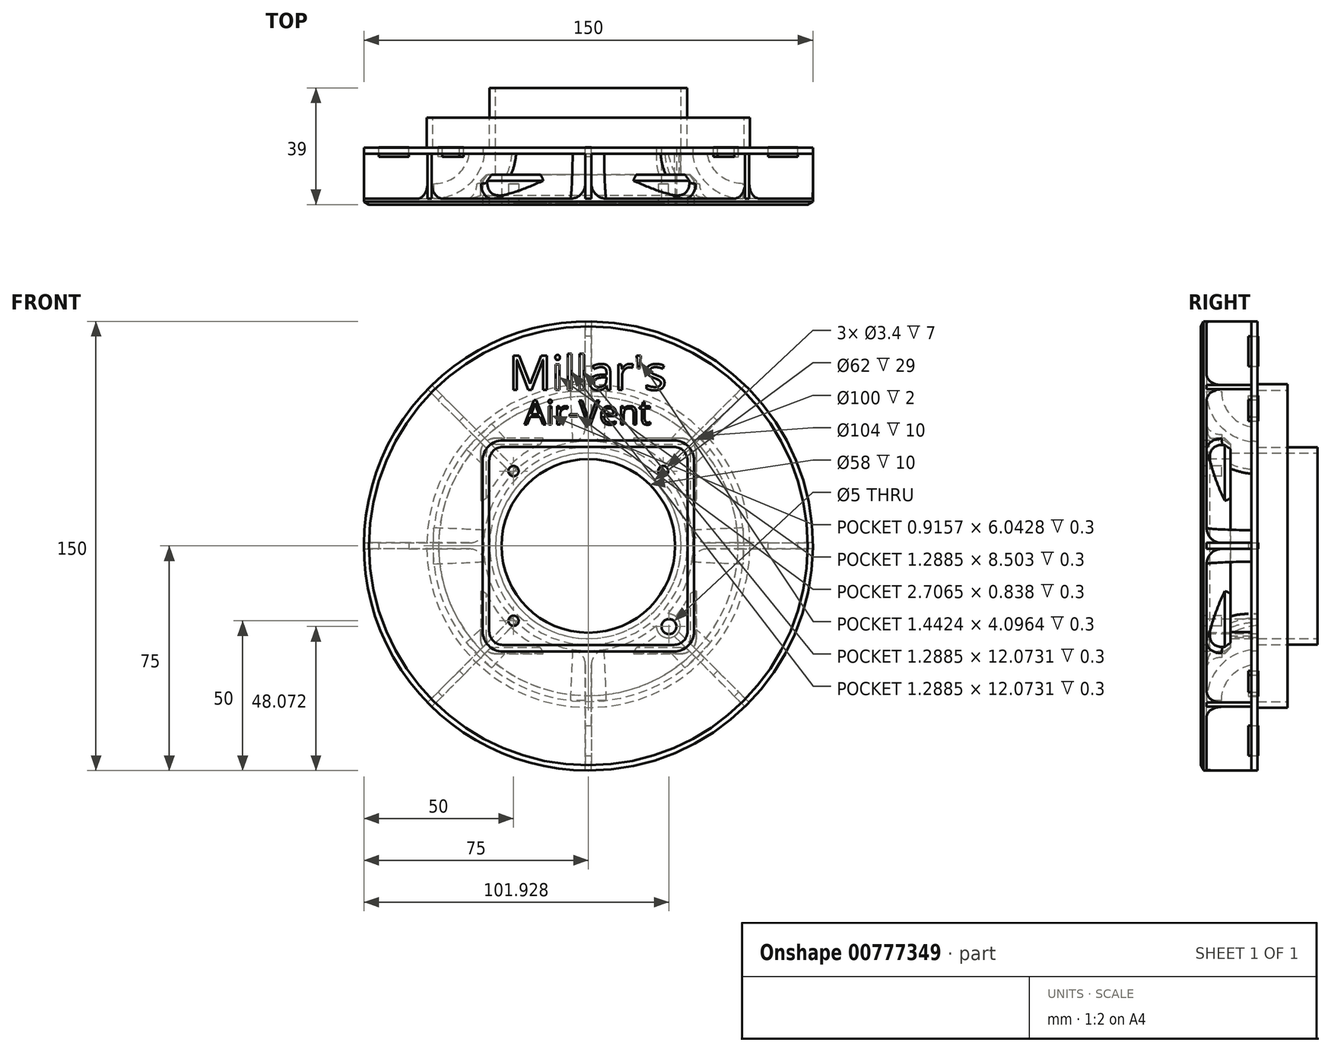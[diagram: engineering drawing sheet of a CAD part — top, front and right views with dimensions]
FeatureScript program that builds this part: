
annotation { "Feature Type Name" : "Feature", "Feature Type Description" : "" }
export const myFeature = defineFeature(function(context is Context, id is Id, definition is map)
    precondition{}
    {
        {
            var Q0;
            Q0=qCreatedBy(makeId("Right.planeOp"),FACE);
            var sketch = newSketch(context, id + "F0", { "sketchPlane" : qUnion([Q0])});
            skLineSegment(sketch, "E0", {"start": v(20, 33) * mm, "end": v(0, 33) * mm});
            skLineSegment(sketch, "E1", {"start": v(0, 33) * mm, "end": v(0, 35) * mm});
            skLineSegment(sketch, "E2", {"start": v(20, 33) * mm, "end": v(20, 31) * mm});
            skLineSegment(sketch, "E3", {"start": v(20, 31) * mm, "end": v(0, 31) * mm});
            skArc(sketch, "E4", {"start": v(0, 35) * mm, "mid": v(-12.02, 39.98) * mm, "end": v(-17, 52) * mm});
            skLineSegment(sketch, "E5", {"start": v(0, 50) * mm, "end": v(0, 52) * mm});
            skLineSegment(sketch, "E6", {"start": v(0, 52) * mm, "end": v(10, 52) * mm});
            skLineSegment(sketch, "E7", {"start": v(10, 52) * mm, "end": v(10, 54) * mm});
            skLineSegment(sketch, "E8", {"start": v(10, 54) * mm, "end": v(0, 54) * mm});
            skLineSegment(sketch, "E9", {"start": v(0, 54) * mm, "end": v(0, 75) * mm});
            skLineSegment(sketch, "E10", {"start": v(0, 75) * mm, "end": v(-2, 75) * mm});
            skLineSegment(sketch, "E11", {"start": v(-2, 75) * mm, "end": v(-2, 50) * mm});
            skLineSegment(sketch, "E12", {"start": v(-2, 50) * mm, "end": v(0, 50) * mm});
            skLineSegment(sketch, "E13", {"start": v(-17, 52) * mm, "end": v(-17, 75) * mm});
            skLineSegment(sketch, "E14", {"start": v(-17, 75) * mm, "end": v(-19, 75) * mm});
            skLineSegment(sketch, "E15", {"start": v(-19, 75) * mm, "end": v(-19, 31) * mm});
            skLineSegment(sketch, "E16", {"start": v(0, 0) * mm, "end": v(-26.64, 0) * mm, "construction": true});
            skLineSegment(sketch, "E17", {"start": v(0, 31) * mm, "end": v(-19, 31) * mm});
            skSolve(sketch);
        }
        {
            var Q0;
            Q0=makeQuery(id+"F0.imprint","IMPRINT",FACE,{"disambiguationData":[TD([[makeQuery(id+"F0.imprint","IMPRINT",EDGE,{"derivedFrom":sQuery(id+"F0.wireOp",EDGE,"E0")}),1.0]])]});
            var Q1;
            Q1=makeQuery(id+"F0.imprint","IMPRINT",FACE,{"disambiguationData":[TD([[makeQuery(id+"F0.imprint","IMPRINT",EDGE,{"derivedFrom":sQuery(id+"F0.wireOp",EDGE,"E5")}),1.0]])]});
            var Q2;
            Q2=sQuery(id+"F0.wireOp",EDGE,"E16");
            revolve(context, id + "F1", {"surfaceOperationType" : NewSurfaceOperationType.NEW, "entities" : qUnion([Q0, Q1]), "axis" : qUnion([Q2]), "revolveType" : RevolveType.FULL});
        }
        {
            var Q0;
            Q0=qCreatedBy(makeId("Front.planeOp"),FACE);
            var Q1;
            Q1 = qBodyType(qCreatedBy(id + "F3" ,EDGE), BodyType.WIRE);
            cPlane(context, id + "F2", {"entities" : qUnion([Q0, Q1]), "cplaneType" : CPlaneType.OFFSET, "offset" : 19 * mm, "width" : 150 * mm, "height" : 150 * mm});
        }
        {
            var Q0;
            Q0=qCreatedBy(id+"F2.planeOp",FACE);
            var sketch = newSketch(context, id + "F3", { "sketchPlane" : qUnion([Q0])});
            skLineSegment(sketch, "E18.bottom", {"start": v(31, 36) * mm, "end": v(-31, 36) * mm});
            skLineSegment(sketch, "E18.top", {"start": v(31, -36) * mm, "end": v(-31, -36) * mm});
            skLineSegment(sketch, "E18.left", {"start": v(36, 31) * mm, "end": v(36, -31) * mm});
            skLineSegment(sketch, "E18.right", {"start": v(-36, 31) * mm, "end": v(-36, -31) * mm});
            skPoint(sketch, "E18.middle", {"position": v(0, 0) * mm});
            skPoint(sketch, "E19.visualSharp", {"position": v(-36, 36) * mm});
            skArc(sketch, "E19.filletArc", {"start": v(-31, 36) * mm, "mid": v(-34.54, 34.54) * mm, "end": v(-36, 31) * mm});
            skPoint(sketch, "E20.visualSharp", {"position": v(36, 36) * mm});
            skArc(sketch, "E20.filletArc", {"start": v(36, 31) * mm, "mid": v(34.54, 34.54) * mm, "end": v(31, 36) * mm});
            skPoint(sketch, "E21.visualSharp", {"position": v(36, -36) * mm});
            skArc(sketch, "E21.filletArc", {"start": v(31, -36) * mm, "mid": v(34.54, -34.54) * mm, "end": v(36, -31) * mm});
            skPoint(sketch, "E22.visualSharp", {"position": v(-36, -36) * mm});
            skArc(sketch, "E22.filletArc", {"start": v(-36, -31) * mm, "mid": v(-34.54, -34.54) * mm, "end": v(-31, -36) * mm});
            skSolve(sketch);
        }
        {
            var Q0;
            Q0=qCreatedBy(id+"F2.planeOp",FACE);
            var sketch = newSketch(context, id + "F4", { "sketchPlane" : qUnion([Q0])});
            skLineSegment(sketch, "E23", {"start": v(0, 0) * mm, "end": v(0, 79.75) * mm, "construction": true});
            skCircle(sketch, "E24", {"center": v(0, 0) * mm, "radius": 35 * mm, "construction": true});
            skCircle(sketch, "E25", {"center": v(0, 0) * mm, "radius": 75 * mm, "construction": true});
            skLineSegment(sketch, "E26", {"start": v(1, 34.99) * mm, "end": v(1, 75) * mm});
            skLineSegment(sketch, "E27", {"start": v(1, 75) * mm, "end": v(-1, 75) * mm});
            skLineSegment(sketch, "E28", {"start": v(-1, 75) * mm, "end": v(-1, 34.99) * mm});
            skLineSegment(sketch, "E29", {"start": v(-1, 34.99) * mm, "end": v(1, 34.99) * mm});
            skLineSegment(sketch, "E30.1.0", {"start": v(-24.03, 25.45) * mm, "end": v(-52.32, 53.74) * mm});
            skLineSegment(sketch, "E30.1.1", {"start": v(-52.32, 53.74) * mm, "end": v(-53.74, 52.32) * mm});
            skLineSegment(sketch, "E30.1.2", {"start": v(-53.74, 52.32) * mm, "end": v(-25.45, 24.03) * mm});
            skLineSegment(sketch, "E30.1.3", {"start": v(-25.45, 24.03) * mm, "end": v(-24.03, 25.45) * mm});
            skLineSegment(sketch, "E30.2.0", {"start": v(-34.99, 1) * mm, "end": v(-75, 1) * mm});
            skLineSegment(sketch, "E30.2.1", {"start": v(-75, 1) * mm, "end": v(-75, -1) * mm});
            skLineSegment(sketch, "E30.2.2", {"start": v(-75, -1) * mm, "end": v(-34.99, -1) * mm});
            skLineSegment(sketch, "E30.2.3", {"start": v(-34.99, -1) * mm, "end": v(-34.99, 1) * mm});
            skLineSegment(sketch, "E30.3.0", {"start": v(-25.45, -24.03) * mm, "end": v(-53.74, -52.32) * mm});
            skLineSegment(sketch, "E30.3.1", {"start": v(-53.74, -52.32) * mm, "end": v(-52.32, -53.74) * mm});
            skLineSegment(sketch, "E30.3.2", {"start": v(-52.32, -53.74) * mm, "end": v(-24.03, -25.45) * mm});
            skLineSegment(sketch, "E30.3.3", {"start": v(-24.03, -25.45) * mm, "end": v(-25.45, -24.03) * mm});
            skLineSegment(sketch, "E30.4.0", {"start": v(-1, -34.99) * mm, "end": v(-1, -75) * mm});
            skLineSegment(sketch, "E30.4.1", {"start": v(-1, -75) * mm, "end": v(1, -75) * mm});
            skLineSegment(sketch, "E30.4.2", {"start": v(1, -75) * mm, "end": v(1, -34.99) * mm});
            skLineSegment(sketch, "E30.4.3", {"start": v(1, -34.99) * mm, "end": v(-1, -34.99) * mm});
            skLineSegment(sketch, "E30.5.0", {"start": v(24.03, -25.45) * mm, "end": v(52.32, -53.74) * mm});
            skLineSegment(sketch, "E30.5.1", {"start": v(52.32, -53.74) * mm, "end": v(53.74, -52.32) * mm});
            skLineSegment(sketch, "E30.5.2", {"start": v(53.74, -52.32) * mm, "end": v(25.45, -24.03) * mm});
            skLineSegment(sketch, "E30.5.3", {"start": v(25.45, -24.03) * mm, "end": v(24.03, -25.45) * mm});
            skLineSegment(sketch, "E30.6.0", {"start": v(34.99, -1) * mm, "end": v(75, -1) * mm});
            skLineSegment(sketch, "E30.6.1", {"start": v(75, -1) * mm, "end": v(75, 1) * mm});
            skLineSegment(sketch, "E30.6.2", {"start": v(75, 1) * mm, "end": v(34.99, 1) * mm});
            skLineSegment(sketch, "E30.6.3", {"start": v(34.99, 1) * mm, "end": v(34.99, -1) * mm});
            skLineSegment(sketch, "E30.7.0", {"start": v(25.45, 24.03) * mm, "end": v(53.74, 52.32) * mm});
            skLineSegment(sketch, "E30.7.1", {"start": v(53.74, 52.32) * mm, "end": v(52.32, 53.74) * mm});
            skLineSegment(sketch, "E30.7.2", {"start": v(52.32, 53.74) * mm, "end": v(24.03, 25.45) * mm});
            skLineSegment(sketch, "E30.7.3", {"start": v(24.03, 25.45) * mm, "end": v(25.45, 24.03) * mm});
            skSolve(sketch);
        }
        {
            var Q0;
            Q0=makeQuery(id+"F4.imprint","IMPRINT",FACE,{"disambiguationData":[TD([[makeQuery(id+"F4.imprint","IMPRINT",EDGE,{"derivedFrom":sQuery(id+"F4.wireOp",EDGE,"E30.1.0")}),1.0]])]});
            var Q1;
            Q1=makeQuery(id+"F4.imprint","IMPRINT",FACE,{"disambiguationData":[TD([[makeQuery(id+"F4.imprint","IMPRINT",EDGE,{"derivedFrom":sQuery(id+"F4.wireOp",EDGE,"E30.2.0")}),1.0]])]});
            var Q2;
            Q2=makeQuery(id+"F4.imprint","IMPRINT",FACE,{"disambiguationData":[TD([[makeQuery(id+"F4.imprint","IMPRINT",EDGE,{"derivedFrom":sQuery(id+"F4.wireOp",EDGE,"E30.3.0")}),1.0]])]});
            var Q3;
            Q3=makeQuery(id+"F4.imprint","IMPRINT",FACE,{"disambiguationData":[TD([[makeQuery(id+"F4.imprint","IMPRINT",EDGE,{"derivedFrom":sQuery(id+"F4.wireOp",EDGE,"E30.4.0")}),1.0]])]});
            var Q4;
            Q4=makeQuery(id+"F4.imprint","IMPRINT",FACE,{"disambiguationData":[TD([[makeQuery(id+"F4.imprint","IMPRINT",EDGE,{"derivedFrom":sQuery(id+"F4.wireOp",EDGE,"E30.5.0")}),1.0]])]});
            var Q5;
            Q5=makeQuery(id+"F4.imprint","IMPRINT",FACE,{"disambiguationData":[TD([[makeQuery(id+"F4.imprint","IMPRINT",EDGE,{"derivedFrom":sQuery(id+"F4.wireOp",EDGE,"E30.6.0")}),1.0]])]});
            var Q6;
            Q6=makeQuery(id+"F4.imprint","IMPRINT",FACE,{"disambiguationData":[TD([[makeQuery(id+"F4.imprint","IMPRINT",EDGE,{"derivedFrom":sQuery(id+"F4.wireOp",EDGE,"E30.7.0")}),1.0]])]});
            var Q7;
            Q7=makeQuery(id+"F4.imprint","IMPRINT",FACE,{"disambiguationData":[TD([[makeQuery(id+"F4.imprint","IMPRINT",EDGE,{"derivedFrom":sQuery(id+"F4.wireOp",EDGE,"E26")}),1.0]])]});
            extrude(context, id + "F5", {"entities" : qUnion([Q0, Q1, Q2, Q3, Q4, Q5, Q6, Q7]), "operationType" : NewBodyOperationType.ADD, "oppositeDirection" : true, "depth" : 17 * mm, "offsetDistance" : 25 * mm});
        }
        {
            var Q0;
            Q0=qCreatedBy(id+"F2.planeOp",FACE);
            cPlane(context, id + "F6", {"entities" : qUnion([Q0]), "cplaneType" : CPlaneType.OFFSET, "offset" : 17 * mm, "oppositeDirection" : true, "width" : 150 * mm, "height" : 150 * mm});
        }
        {
            var Q0;
            Q0=qCreatedBy(id+"F6.planeOp",FACE);
            var sketch = newSketch(context, id + "F7", { "sketchPlane" : qUnion([Q0])});
            skLineSegment(sketch, "E31", {"start": v(0, 0) * mm, "end": v(0, 49.28) * mm, "construction": true});
            skLineSegment(sketch, "E32.bottom", {"start": v(-1, 60) * mm, "end": v(1, 60) * mm});
            skLineSegment(sketch, "E32.top", {"start": v(-1, 70) * mm, "end": v(1, 70) * mm});
            skLineSegment(sketch, "E32.left", {"start": v(-1, 60) * mm, "end": v(-1, 70) * mm});
            skLineSegment(sketch, "E32.right", {"start": v(1, 60) * mm, "end": v(1, 70) * mm});
            skPoint(sketch, "E32.middle", {"position": v(0, 65) * mm});
            skLineSegment(sketch, "E33.1.0", {"start": v(-41.72, 43.13) * mm, "end": v(-48.8, 50.2) * mm});
            skLineSegment(sketch, "E33.1.1", {"start": v(-50.2, 48.8) * mm, "end": v(-48.8, 50.2) * mm});
            skLineSegment(sketch, "E33.1.2", {"start": v(-43.13, 41.72) * mm, "end": v(-50.2, 48.8) * mm});
            skLineSegment(sketch, "E33.1.3", {"start": v(-43.13, 41.72) * mm, "end": v(-41.72, 43.13) * mm});
            skLineSegment(sketch, "E33.2.0", {"start": v(-60, 1) * mm, "end": v(-70, 1) * mm});
            skLineSegment(sketch, "E33.2.1", {"start": v(-70, -1) * mm, "end": v(-70, 1) * mm});
            skLineSegment(sketch, "E33.2.2", {"start": v(-60, -1) * mm, "end": v(-70, -1) * mm});
            skLineSegment(sketch, "E33.2.3", {"start": v(-60, -1) * mm, "end": v(-60, 1) * mm});
            skLineSegment(sketch, "E33.3.0", {"start": v(-43.13, -41.72) * mm, "end": v(-50.2, -48.8) * mm});
            skLineSegment(sketch, "E33.3.1", {"start": v(-48.8, -50.2) * mm, "end": v(-50.2, -48.8) * mm});
            skLineSegment(sketch, "E33.3.2", {"start": v(-41.72, -43.13) * mm, "end": v(-48.8, -50.2) * mm});
            skLineSegment(sketch, "E33.3.3", {"start": v(-41.72, -43.13) * mm, "end": v(-43.13, -41.72) * mm});
            skLineSegment(sketch, "E33.4.0", {"start": v(-1, -60) * mm, "end": v(-1, -70) * mm});
            skLineSegment(sketch, "E33.4.1", {"start": v(1, -70) * mm, "end": v(-1, -70) * mm});
            skLineSegment(sketch, "E33.4.2", {"start": v(1, -60) * mm, "end": v(1, -70) * mm});
            skLineSegment(sketch, "E33.4.3", {"start": v(1, -60) * mm, "end": v(-1, -60) * mm});
            skLineSegment(sketch, "E33.5.0", {"start": v(41.72, -43.13) * mm, "end": v(48.8, -50.2) * mm});
            skLineSegment(sketch, "E33.5.1", {"start": v(50.2, -48.8) * mm, "end": v(48.8, -50.2) * mm});
            skLineSegment(sketch, "E33.5.2", {"start": v(43.13, -41.72) * mm, "end": v(50.2, -48.8) * mm});
            skLineSegment(sketch, "E33.5.3", {"start": v(43.13, -41.72) * mm, "end": v(41.72, -43.13) * mm});
            skLineSegment(sketch, "E33.6.0", {"start": v(60, -1) * mm, "end": v(70, -1) * mm});
            skLineSegment(sketch, "E33.6.1", {"start": v(70, 1) * mm, "end": v(70, -1) * mm});
            skLineSegment(sketch, "E33.6.2", {"start": v(60, 1) * mm, "end": v(70, 1) * mm});
            skLineSegment(sketch, "E33.6.3", {"start": v(60, 1) * mm, "end": v(60, -1) * mm});
            skLineSegment(sketch, "E33.7.0", {"start": v(43.13, 41.72) * mm, "end": v(50.2, 48.8) * mm});
            skLineSegment(sketch, "E33.7.1", {"start": v(48.8, 50.2) * mm, "end": v(50.2, 48.8) * mm});
            skLineSegment(sketch, "E33.7.2", {"start": v(41.72, 43.13) * mm, "end": v(48.8, 50.2) * mm});
            skLineSegment(sketch, "E33.7.3", {"start": v(41.72, 43.13) * mm, "end": v(43.13, 41.72) * mm});
            skPoint(sketch, "E33.center", {"position": v(0, 0) * mm});
            skSolve(sketch);
        }
        {
            var Q0;
            Q0=makeQuery(id+"F7.imprint","IMPRINT",FACE,{"disambiguationData":[TD([[makeQuery(id+"F7.imprint","IMPRINT",EDGE,{"derivedFrom":sQuery(id+"F7.wireOp",EDGE,"E32.bottom")}),1.0]])]});
            var Q1;
            Q1=makeQuery(id+"F7.imprint","IMPRINT",FACE,{"disambiguationData":[TD([[makeQuery(id+"F7.imprint","IMPRINT",EDGE,{"derivedFrom":sQuery(id+"F7.wireOp",EDGE,"E33.7.0")}),1.0]])]});
            var Q2;
            Q2=makeQuery(id+"F7.imprint","IMPRINT",FACE,{"disambiguationData":[TD([[makeQuery(id+"F7.imprint","IMPRINT",EDGE,{"derivedFrom":sQuery(id+"F7.wireOp",EDGE,"E33.6.0")}),1.0]])]});
            var Q3;
            Q3=makeQuery(id+"F7.imprint","IMPRINT",FACE,{"disambiguationData":[TD([[makeQuery(id+"F7.imprint","IMPRINT",EDGE,{"derivedFrom":sQuery(id+"F7.wireOp",EDGE,"E33.1.0")}),1.0]])]});
            var Q4;
            Q4=makeQuery(id+"F7.imprint","IMPRINT",FACE,{"disambiguationData":[TD([[makeQuery(id+"F7.imprint","IMPRINT",EDGE,{"derivedFrom":sQuery(id+"F7.wireOp",EDGE,"E33.2.0")}),1.0]])]});
            var Q5;
            Q5=makeQuery(id+"F7.imprint","IMPRINT",FACE,{"disambiguationData":[TD([[makeQuery(id+"F7.imprint","IMPRINT",EDGE,{"derivedFrom":sQuery(id+"F7.wireOp",EDGE,"E33.3.0")}),1.0]])]});
            var Q6;
            Q6=makeQuery(id+"F7.imprint","IMPRINT",FACE,{"disambiguationData":[TD([[makeQuery(id+"F7.imprint","IMPRINT",EDGE,{"derivedFrom":sQuery(id+"F7.wireOp",EDGE,"E33.4.0")}),1.0]])]});
            var Q7;
            Q7=makeQuery(id+"F7.imprint","IMPRINT",FACE,{"disambiguationData":[TD([[makeQuery(id+"F7.imprint","IMPRINT",EDGE,{"derivedFrom":sQuery(id+"F7.wireOp",EDGE,"E33.5.0")}),1.0]])]});
            extrude(context, id + "F8", {"entities" : qUnion([Q0, Q1, Q2, Q3, Q4, Q5, Q6, Q7]), "operationType" : NewBodyOperationType.ADD, "oppositeDirection" : true, "depth" : 2.2 * mm, "offsetDistance" : 25 * mm});
        }
        {
            var Q0;
            Q0=makeQuery(id+"F3.imprint","IMPRINT",FACE,{"disambiguationData":[TD([[makeQuery(id+"F3.imprint","IMPRINT",EDGE,{"derivedFrom":sQuery(id+"F3.wireOp",EDGE,"E18.bottom")}),1.0]])]});
            extrude(context, id + "F9", {"entities" : qUnion([Q0]), "operationType" : NewBodyOperationType.ADD, "oppositeDirection" : true, "depth" : 10 * mm, "offsetDistance" : 25 * mm});
        }
        {
            var Q0;
            Q0=qCreatedBy(makeId("Front.planeOp"),FACE);
            cPlane(context, id + "F10", {"entities" : qUnion([Q0]), "cplaneType" : CPlaneType.OFFSET, "offset" : 19 * mm, "width" : 150 * mm, "height" : 150 * mm});
        }
        {
            var Q0;
            Q0=qCreatedBy(id+"F10.planeOp",FACE);
            var sketch = newSketch(context, id + "F11", { "sketchPlane" : qUnion([Q0])});
            skLineSegment(sketch, "E34", {"start": v(0, 0) * mm, "end": v(-52.1, 52.1) * mm, "construction": true});
            skLineSegment(sketch, "E35", {"start": v(-52.1, 52.1) * mm, "end": v(0, 0) * mm, "construction": true});
            skLineSegment(sketch, "E36", {"start": v(0, 0) * mm, "end": v(53.31, 53.31) * mm, "construction": true});
            skLineSegment(sketch, "E37", {"start": v(0, 0) * mm, "end": v(0, 62.57) * mm, "construction": true});
            skCircle(sketch, "E38", {"center": v(-25, 25) * mm, "radius": 1.7 * mm});
            skCircle(sketch, "E39.1.0", {"center": v(-25, -25) * mm, "radius": 1.7 * mm});
            skCircle(sketch, "E39.3.0", {"center": v(25, 25) * mm, "radius": 1.7 * mm});
            skPoint(sketch, "E39.center", {"position": v(0, 0) * mm});
            skSolve(sketch);
        }
        {
            var Q0;
            Q0=makeQuery(id+"F11.imprint","IMPRINT",FACE,{"disambiguationData":[TD([[makeQuery(id+"F11.imprint","IMPRINT",EDGE,{"derivedFrom":sQuery(id+"F11.wireOp",EDGE,"E38")}),1.0]])]});
            var Q1;
            Q1=makeQuery(id+"F11.imprint","IMPRINT",FACE,{"disambiguationData":[TD([[makeQuery(id+"F11.imprint","IMPRINT",EDGE,{"derivedFrom":sQuery(id+"F11.wireOp",EDGE,"E39.3.0")}),1.0]])]});
            var Q2;
            Q2=makeQuery(id+"F11.imprint","IMPRINT",FACE,{"disambiguationData":[TD([[makeQuery(id+"F11.imprint","IMPRINT",EDGE,{"derivedFrom":sQuery(id+"F11.wireOp",EDGE,"E39.2.0")}),1.0]])]});
            var Q3;
            Q3=makeQuery(id+"F11.imprint","IMPRINT",FACE,{"disambiguationData":[TD([[makeQuery(id+"F11.imprint","IMPRINT",EDGE,{"derivedFrom":sQuery(id+"F11.wireOp",EDGE,"E39.1.0")}),1.0]])]});
            extrude(context, id + "F12", {"entities" : qUnion([Q0, Q1, Q2, Q3]), "operationType" : NewBodyOperationType.REMOVE, "oppositeDirection" : true, "depth" : 7 * mm, "offsetDistance" : 25 * mm});
        }
        {
            var Q0;
            Q0=qCreatedBy(id+"F10.planeOp",FACE);
            var sketch = newSketch(context, id + "F13", { "sketchPlane" : qUnion([Q0])});
            skCircle(sketch, "E40", {"center": v(0, 0) * mm, "radius": 29 * mm});
            skSolve(sketch);
        }
        {
            var Q0;
            Q0=makeQuery(id+"F13.imprint","IMPRINT",FACE,{"disambiguationData":[TD([[makeQuery(id+"F13.imprint","IMPRINT",EDGE,{"derivedFrom":sQuery(id+"F13.wireOp",EDGE,"E40")}),1.0]])]});
            extrude(context, id + "F14", {"entities" : qUnion([Q0]), "operationType" : NewBodyOperationType.REMOVE, "oppositeDirection" : true, "depth" : 10 * mm, "offsetDistance" : 25 * mm});
        }
        {
            var Q0;
            Q0=makeQuery(id+"F14.boolean.opBoolean","COPY",EDGE,{"derivedFrom":makeQuery(id+"F14.opExtrude","CAP_EDGE",EDGE,{"disambiguationData":[OSD([sQuery(id+"F13.wireOp",EDGE,"E40")])],"isStart":false})});
            var Q1;
            Q1=makeQuery(id+"F9.opExtrude","CAP_EDGE",EDGE,{"disambiguationData":[OSD([sQuery(id+"F3.wireOp",EDGE,"E19.filletArc")])],"isStart":false});
            var Q2;
            Q2=makeQuery(id+"F9.opExtrude","CAP_EDGE",EDGE,{"disambiguationData":[OSD([sQuery(id+"F3.wireOp",EDGE,"E20.filletArc")])],"isStart":false});
            var Q3;
            Q3=makeQuery(id+"F9.opExtrude","CAP_EDGE",EDGE,{"disambiguationData":[OSD([sQuery(id+"F3.wireOp",EDGE,"E21.filletArc")])],"isStart":false});
            var Q4;
            Q4=makeQuery(id+"F9.opExtrude","CAP_EDGE",EDGE,{"disambiguationData":[OSD([sQuery(id+"F3.wireOp",EDGE,"E22.filletArc")])],"isStart":false});
            chamfer(context, id + "F15", {"entities" : qUnion([Q0, Q1, Q2, Q3, Q4]), "width" : 2 * mm, "tangentPropagation" : true});
        }
        {
            var Q0;
            Q0=makeQuery(id+"F1.opRevolve","SWEPT_EDGE",EDGE,{"disambiguationData":[OSD([sQuery(id+"F0.wireOp",EDGE,"E14"),sQuery(id+"F0.wireOp",EDGE,"E15")])]});
            chamfer(context, id + "F16", {"entities" : qUnion([Q0]), "chamferType" : ChamferType.OFFSET_ANGLE, "width" : 1 * mm, "oppositeDirection" : false, "angle" : 60 * degree, "tangentPropagation" : true});
        }
        {
            var Q0;
            Q0=qCreatedBy(makeId("Front.planeOp"),FACE);
            var sketch = newSketch(context, id + "F17", { "sketchPlane" : qUnion([Q0])});
            skLineSegment(sketch, "E41", {"start": v(0, 0) * mm, "end": v(0, 49.28) * mm, "construction": true});
            skLineSegment(sketch, "E42.bottom", {"start": v(-1, 60) * mm, "end": v(1, 60) * mm});
            skLineSegment(sketch, "E42.top", {"start": v(-1, 70) * mm, "end": v(1, 70) * mm});
            skLineSegment(sketch, "E42.left", {"start": v(-1, 60) * mm, "end": v(-1, 70) * mm});
            skLineSegment(sketch, "E42.right", {"start": v(1, 60) * mm, "end": v(1, 70) * mm});
            skPoint(sketch, "E42.middle", {"position": v(0, 65) * mm});
            skLineSegment(sketch, "E43.1.0", {"start": v(-41.72, 43.13) * mm, "end": v(-48.8, 50.2) * mm});
            skLineSegment(sketch, "E43.1.1", {"start": v(-50.2, 48.8) * mm, "end": v(-48.8, 50.2) * mm});
            skLineSegment(sketch, "E43.1.2", {"start": v(-43.13, 41.72) * mm, "end": v(-50.2, 48.8) * mm});
            skLineSegment(sketch, "E43.1.3", {"start": v(-43.13, 41.72) * mm, "end": v(-41.72, 43.13) * mm});
            skLineSegment(sketch, "E43.2.0", {"start": v(-60, 1) * mm, "end": v(-70, 1) * mm});
            skLineSegment(sketch, "E43.2.1", {"start": v(-70, -1) * mm, "end": v(-70, 1) * mm});
            skLineSegment(sketch, "E43.2.2", {"start": v(-60, -1) * mm, "end": v(-70, -1) * mm});
            skLineSegment(sketch, "E43.2.3", {"start": v(-60, -1) * mm, "end": v(-60, 1) * mm});
            skLineSegment(sketch, "E43.3.0", {"start": v(-43.13, -41.72) * mm, "end": v(-50.2, -48.8) * mm});
            skLineSegment(sketch, "E43.3.1", {"start": v(-48.8, -50.2) * mm, "end": v(-50.2, -48.8) * mm});
            skLineSegment(sketch, "E43.3.2", {"start": v(-41.72, -43.13) * mm, "end": v(-48.8, -50.2) * mm});
            skLineSegment(sketch, "E43.3.3", {"start": v(-41.72, -43.13) * mm, "end": v(-43.13, -41.72) * mm});
            skLineSegment(sketch, "E43.4.0", {"start": v(-1, -60) * mm, "end": v(-1, -70) * mm});
            skLineSegment(sketch, "E43.4.1", {"start": v(1, -70) * mm, "end": v(-1, -70) * mm});
            skLineSegment(sketch, "E43.4.2", {"start": v(1, -60) * mm, "end": v(1, -70) * mm});
            skLineSegment(sketch, "E43.4.3", {"start": v(1, -60) * mm, "end": v(-1, -60) * mm});
            skLineSegment(sketch, "E43.5.0", {"start": v(41.72, -43.13) * mm, "end": v(48.8, -50.2) * mm});
            skLineSegment(sketch, "E43.5.1", {"start": v(50.2, -48.8) * mm, "end": v(48.8, -50.2) * mm});
            skLineSegment(sketch, "E43.5.2", {"start": v(43.13, -41.72) * mm, "end": v(50.2, -48.8) * mm});
            skLineSegment(sketch, "E43.5.3", {"start": v(43.13, -41.72) * mm, "end": v(41.72, -43.13) * mm});
            skLineSegment(sketch, "E43.6.0", {"start": v(60, -1) * mm, "end": v(70, -1) * mm});
            skLineSegment(sketch, "E43.6.1", {"start": v(70, 1) * mm, "end": v(70, -1) * mm});
            skLineSegment(sketch, "E43.6.2", {"start": v(60, 1) * mm, "end": v(70, 1) * mm});
            skLineSegment(sketch, "E43.6.3", {"start": v(60, 1) * mm, "end": v(60, -1) * mm});
            skLineSegment(sketch, "E43.7.0", {"start": v(43.13, 41.72) * mm, "end": v(50.2, 48.8) * mm});
            skLineSegment(sketch, "E43.7.1", {"start": v(48.8, 50.2) * mm, "end": v(50.2, 48.8) * mm});
            skLineSegment(sketch, "E43.7.2", {"start": v(41.72, 43.13) * mm, "end": v(48.8, 50.2) * mm});
            skLineSegment(sketch, "E43.7.3", {"start": v(41.72, 43.13) * mm, "end": v(43.13, 41.72) * mm});
            skPoint(sketch, "E43.center", {"position": v(0, 0) * mm});
            skSolve(sketch);
        }
        {
            var Q0;
            Q0=makeQuery(id+"F17.imprint","IMPRINT",FACE,{"disambiguationData":[TD([[makeQuery(id+"F17.imprint","IMPRINT",EDGE,{"derivedFrom":sQuery(id+"F17.wireOp",EDGE,"E42.bottom")}),1.0]])]});
            var Q1;
            Q1=makeQuery(id+"F17.imprint","IMPRINT",FACE,{"disambiguationData":[TD([[makeQuery(id+"F17.imprint","IMPRINT",EDGE,{"derivedFrom":sQuery(id+"F17.wireOp",EDGE,"E43.7.0")}),1.0]])]});
            var Q2;
            Q2=makeQuery(id+"F17.imprint","IMPRINT",FACE,{"disambiguationData":[TD([[makeQuery(id+"F17.imprint","IMPRINT",EDGE,{"derivedFrom":sQuery(id+"F17.wireOp",EDGE,"E43.6.0")}),1.0]])]});
            var Q3;
            Q3=makeQuery(id+"F17.imprint","IMPRINT",FACE,{"disambiguationData":[TD([[makeQuery(id+"F17.imprint","IMPRINT",EDGE,{"derivedFrom":sQuery(id+"F17.wireOp",EDGE,"E43.5.0")}),1.0]])]});
            var Q4;
            Q4=makeQuery(id+"F17.imprint","IMPRINT",FACE,{"disambiguationData":[TD([[makeQuery(id+"F17.imprint","IMPRINT",EDGE,{"derivedFrom":sQuery(id+"F17.wireOp",EDGE,"E43.4.0")}),1.0]])]});
            var Q5;
            Q5=makeQuery(id+"F17.imprint","IMPRINT",FACE,{"disambiguationData":[TD([[makeQuery(id+"F17.imprint","IMPRINT",EDGE,{"derivedFrom":sQuery(id+"F17.wireOp",EDGE,"E43.3.0")}),1.0]])]});
            var Q6;
            Q6=makeQuery(id+"F17.imprint","IMPRINT",FACE,{"disambiguationData":[TD([[makeQuery(id+"F17.imprint","IMPRINT",EDGE,{"derivedFrom":sQuery(id+"F17.wireOp",EDGE,"E43.2.0")}),1.0]])]});
            var Q7;
            Q7=makeQuery(id+"F17.imprint","IMPRINT",FACE,{"disambiguationData":[TD([[makeQuery(id+"F17.imprint","IMPRINT",EDGE,{"derivedFrom":sQuery(id+"F17.wireOp",EDGE,"E43.1.0")}),1.0]])]});
            extrude(context, id + "F18", {"entities" : qUnion([Q0, Q1, Q2, Q3, Q4, Q5, Q6, Q7]), "operationType" : NewBodyOperationType.REMOVE, "depth" : 3 * mm, "offsetDistance" : 25 * mm});
        }
        {
            var Q0;
            Q0=qCreatedBy(makeId("Front.planeOp"),FACE);
            cPlane(context, id + "F19", {"entities" : qUnion([Q0]), "cplaneType" : CPlaneType.OFFSET, "offset" : 20 * mm, "width" : 150 * mm, "height" : 150 * mm});
        }
        {
            var Q0;
            Q0=qCreatedBy(id+"F19.planeOp",FACE);
            var sketch = newSketch(context, id + "F20", { "sketchPlane" : qUnion([Q0])});
            skLineSegment(sketch, "E44.bottom", {"start": v(28.6, 33.05) * mm, "end": v(-28.6, 33.05) * mm});
            skLineSegment(sketch, "E44.top", {"start": v(28.6, -33.05) * mm, "end": v(-28.6, -33.05) * mm});
            skLineSegment(sketch, "E44.left", {"start": v(33.1, 28.55) * mm, "end": v(33.1, -28.55) * mm});
            skLineSegment(sketch, "E44.right", {"start": v(-33.1, 28.55) * mm, "end": v(-33.1, -28.55) * mm});
            skPoint(sketch, "E44.middle", {"position": v(0, 0) * mm});
            skPoint(sketch, "E45.visualSharp", {"position": v(-33.1, 33.05) * mm});
            skArc(sketch, "E45.filletArc", {"start": v(-28.6, 33.05) * mm, "mid": v(-31.78, 31.73) * mm, "end": v(-33.1, 28.55) * mm});
            skPoint(sketch, "E46.visualSharp", {"position": v(33.1, 33.05) * mm});
            skArc(sketch, "E46.filletArc", {"start": v(33.1, 28.55) * mm, "mid": v(31.78, 31.73) * mm, "end": v(28.6, 33.05) * mm});
            skPoint(sketch, "E47.visualSharp", {"position": v(33.1, -33.05) * mm});
            skArc(sketch, "E47.filletArc", {"start": v(28.6, -33.05) * mm, "mid": v(31.78, -31.73) * mm, "end": v(33.1, -28.55) * mm});
            skPoint(sketch, "E48.visualSharp", {"position": v(-33.1, -33.05) * mm});
            skArc(sketch, "E48.filletArc", {"start": v(-33.1, -28.55) * mm, "mid": v(-31.78, -31.73) * mm, "end": v(-28.6, -33.05) * mm});
            skArc(sketch, "E49.0", {"start": v(35.3, 28.55) * mm, "mid": v(33.34, 33.29) * mm, "end": v(28.6, 35.25) * mm});
            skLineSegment(sketch, "E49.1", {"start": v(35.3, 28.55) * mm, "end": v(35.3, -28.55) * mm});
            skLineSegment(sketch, "E49.2", {"start": v(28.6, 35.25) * mm, "end": v(-28.6, 35.25) * mm});
            skArc(sketch, "E49.3", {"start": v(28.6, -35.25) * mm, "mid": v(33.34, -33.29) * mm, "end": v(35.3, -28.55) * mm});
            skArc(sketch, "E49.4", {"start": v(-28.6, 35.25) * mm, "mid": v(-33.34, 33.29) * mm, "end": v(-35.3, 28.55) * mm});
            skLineSegment(sketch, "E49.5", {"start": v(-35.3, 28.55) * mm, "end": v(-35.3, -28.55) * mm});
            skArc(sketch, "E49.6", {"start": v(-35.3, -28.55) * mm, "mid": v(-33.34, -33.29) * mm, "end": v(-28.6, -35.25) * mm});
            skLineSegment(sketch, "E49.7", {"start": v(28.6, -35.25) * mm, "end": v(-28.6, -35.25) * mm});
            skSolve(sketch);
        }
        {
            var Q0;
            Q0 = qSketchRegion(id + "F20", true);
            extrude(context, id + "F21", {"entities" : qUnion([Q0]), "operationType" : NewBodyOperationType.REMOVE, "oppositeDirection" : true, "depth" : 4 * mm, "offsetDistance" : 25 * mm});
        }
        {
            var Q0;
            Q0=makeQuery(id+"F5.boolean.opBoolean","INTERSECT",EDGE,{"derivedFrom":[makeQuery(id+"F1.opRevolve","SWEPT_FACE",FACE,{"disambiguationData":[OSD([sQuery(id+"F0.wireOp",EDGE,"E13")])]}),makeQuery(id+"F5.opExtrude","SWEPT_FACE",FACE,{"disambiguationData":[OSD([sQuery(id+"F4.wireOp",EDGE,"E30.7.0")])]})]});
            var Q1;
            Q1=makeQuery(id+"F5.boolean.opBoolean","INTERSECT",EDGE,{"derivedFrom":[makeQuery(id+"F1.opRevolve","SWEPT_FACE",FACE,{"disambiguationData":[OSD([sQuery(id+"F0.wireOp",EDGE,"E13")])]}),makeQuery(id+"F5.opExtrude","SWEPT_FACE",FACE,{"disambiguationData":[OSD([sQuery(id+"F4.wireOp",EDGE,"E26")])]})]});
            var Q2;
            Q2=makeQuery(id+"F5.boolean.opBoolean","INTERSECT",EDGE,{"derivedFrom":[makeQuery(id+"F1.opRevolve","SWEPT_FACE",FACE,{"disambiguationData":[OSD([sQuery(id+"F0.wireOp",EDGE,"E13")])]}),makeQuery(id+"F5.opExtrude","SWEPT_FACE",FACE,{"disambiguationData":[OSD([sQuery(id+"F4.wireOp",EDGE,"E30.6.0")])]})]});
            var Q3;
            Q3=makeQuery(id+"F5.boolean.opBoolean","INTERSECT",EDGE,{"derivedFrom":[makeQuery(id+"F1.opRevolve","SWEPT_FACE",FACE,{"disambiguationData":[OSD([sQuery(id+"F0.wireOp",EDGE,"E13")])]}),makeQuery(id+"F5.opExtrude","SWEPT_FACE",FACE,{"disambiguationData":[OSD([sQuery(id+"F4.wireOp",EDGE,"E30.5.2")])]})]});
            var Q4;
            Q4=makeQuery(id+"F5.boolean.opBoolean","INTERSECT",EDGE,{"derivedFrom":[makeQuery(id+"F1.opRevolve","SWEPT_FACE",FACE,{"disambiguationData":[OSD([sQuery(id+"F0.wireOp",EDGE,"E13")])]}),makeQuery(id+"F5.opExtrude","SWEPT_FACE",FACE,{"disambiguationData":[OSD([sQuery(id+"F4.wireOp",EDGE,"E30.4.2")])]})]});
            var Q5;
            Q5=makeQuery(id+"F5.boolean.opBoolean","INTERSECT",EDGE,{"derivedFrom":[makeQuery(id+"F1.opRevolve","SWEPT_FACE",FACE,{"disambiguationData":[OSD([sQuery(id+"F0.wireOp",EDGE,"E13")])]}),makeQuery(id+"F5.opExtrude","SWEPT_FACE",FACE,{"disambiguationData":[OSD([sQuery(id+"F4.wireOp",EDGE,"E30.3.2")])]})]});
            var Q6;
            Q6=makeQuery(id+"F5.boolean.opBoolean","INTERSECT",EDGE,{"derivedFrom":[makeQuery(id+"F1.opRevolve","SWEPT_FACE",FACE,{"disambiguationData":[OSD([sQuery(id+"F0.wireOp",EDGE,"E13")])]}),makeQuery(id+"F5.opExtrude","SWEPT_FACE",FACE,{"disambiguationData":[OSD([sQuery(id+"F4.wireOp",EDGE,"E30.2.2")])]})]});
            var Q7;
            Q7=makeQuery(id+"F5.boolean.opBoolean","INTERSECT",EDGE,{"derivedFrom":[makeQuery(id+"F1.opRevolve","SWEPT_FACE",FACE,{"disambiguationData":[OSD([sQuery(id+"F0.wireOp",EDGE,"E13")])]}),makeQuery(id+"F5.opExtrude","SWEPT_FACE",FACE,{"disambiguationData":[OSD([sQuery(id+"F4.wireOp",EDGE,"E30.1.0")])]})]});
            var Q8;
            Q8=makeQuery(id+"F5.boolean.opBoolean","INTERSECT",EDGE,{"derivedFrom":[makeQuery(id+"F1.opRevolve","SWEPT_FACE",FACE,{"disambiguationData":[OSD([sQuery(id+"F0.wireOp",EDGE,"E13")])]}),makeQuery(id+"F5.opExtrude","SWEPT_FACE",FACE,{"disambiguationData":[OSD([sQuery(id+"F4.wireOp",EDGE,"E30.6.2")])]})]});
            var Q9;
            Q9=makeQuery(id+"F5.boolean.opBoolean","INTERSECT",EDGE,{"derivedFrom":[makeQuery(id+"F1.opRevolve","SWEPT_FACE",FACE,{"disambiguationData":[OSD([sQuery(id+"F0.wireOp",EDGE,"E13")])]}),makeQuery(id+"F5.opExtrude","SWEPT_FACE",FACE,{"disambiguationData":[OSD([sQuery(id+"F4.wireOp",EDGE,"E30.7.2")])]})]});
            var Q10;
            Q10=makeQuery(id+"F5.boolean.opBoolean","INTERSECT",EDGE,{"derivedFrom":[makeQuery(id+"F1.opRevolve","SWEPT_FACE",FACE,{"disambiguationData":[OSD([sQuery(id+"F0.wireOp",EDGE,"E13")])]}),makeQuery(id+"F5.opExtrude","SWEPT_FACE",FACE,{"disambiguationData":[OSD([sQuery(id+"F4.wireOp",EDGE,"E30.2.0")])]})]});
            var Q11;
            Q11=makeQuery(id+"F5.boolean.opBoolean","INTERSECT",EDGE,{"derivedFrom":[makeQuery(id+"F1.opRevolve","SWEPT_FACE",FACE,{"disambiguationData":[OSD([sQuery(id+"F0.wireOp",EDGE,"E13")])]}),makeQuery(id+"F5.opExtrude","SWEPT_FACE",FACE,{"disambiguationData":[OSD([sQuery(id+"F4.wireOp",EDGE,"E30.3.0")])]})]});
            var Q12;
            Q12=makeQuery(id+"F5.boolean.opBoolean","INTERSECT",EDGE,{"derivedFrom":[makeQuery(id+"F1.opRevolve","SWEPT_FACE",FACE,{"disambiguationData":[OSD([sQuery(id+"F0.wireOp",EDGE,"E13")])]}),makeQuery(id+"F5.opExtrude","SWEPT_FACE",FACE,{"disambiguationData":[OSD([sQuery(id+"F4.wireOp",EDGE,"E30.5.0")])]})]});
            var Q13;
            Q13=makeQuery(id+"F5.boolean.opBoolean","INTERSECT",EDGE,{"derivedFrom":[makeQuery(id+"F1.opRevolve","SWEPT_FACE",FACE,{"disambiguationData":[OSD([sQuery(id+"F0.wireOp",EDGE,"E13")])]}),makeQuery(id+"F5.opExtrude","SWEPT_FACE",FACE,{"disambiguationData":[OSD([sQuery(id+"F4.wireOp",EDGE,"E30.4.0")])]})]});
            var Q14;
            Q14=makeQuery(id+"F5.boolean.opBoolean","INTERSECT",EDGE,{"derivedFrom":[makeQuery(id+"F1.opRevolve","SWEPT_FACE",FACE,{"disambiguationData":[OSD([sQuery(id+"F0.wireOp",EDGE,"E13")])]}),makeQuery(id+"F5.opExtrude","SWEPT_FACE",FACE,{"disambiguationData":[OSD([sQuery(id+"F4.wireOp",EDGE,"E30.1.2")])]})]});
            var Q15;
            Q15=makeQuery(id+"F5.boolean.opBoolean","INTERSECT",EDGE,{"derivedFrom":[makeQuery(id+"F1.opRevolve","SWEPT_FACE",FACE,{"disambiguationData":[OSD([sQuery(id+"F0.wireOp",EDGE,"E13")])]}),makeQuery(id+"F5.opExtrude","SWEPT_FACE",FACE,{"disambiguationData":[OSD([sQuery(id+"F4.wireOp",EDGE,"E28")])]})]});
            fillet(context, id + "F22", {"entities" : qUnion([Q0, Q1, Q2, Q3, Q4, Q5, Q6, Q7, Q8, Q9, Q10, Q11, Q12, Q13, Q14, Q15]), "radius" : 5 * mm, "tangentPropagation" : true, "allowEdgeOverflow" : false});
        }
        {
            var Q0;
            Q0=qCreatedBy(makeId("Front.planeOp"),FACE);
            cPlane(context, id + "F23", {"entities" : qUnion([Q0]), "cplaneType" : CPlaneType.OFFSET, "offset" : 19 * mm, "width" : 150 * mm, "height" : 150 * mm});
        }
        {
            var Q0;
            Q0=qCreatedBy(id+"F23.planeOp",FACE);
            var sketch = newSketch(context, id + "F24", { "sketchPlane" : qUnion([Q0])});
            skText(sketch, "E50", { "text": "Air-Vent", "fontName": "OpenSans-Regular.ttf"});
            skText(sketch, "E51", { "text": "Millar\'s", "fontName": "OpenSans-Regular.ttf"});
            const initialGuessF24  = {"E50": [-0.02135, 0.04056, 1, 0, 0.00813], "E51": [-0.02664, 0.05214, 1, 0, 0.01144]};
            skSetInitialGuess(sketch, initialGuessF24);
            skSolve(sketch);
        }
        {
            var Q0;
            Q0 = qSketchRegion(id + "F24", true);
            extrude(context, id + "F25", {"entities" : qUnion([Q0]), "operationType" : NewBodyOperationType.REMOVE, "oppositeDirection" : true, "depth" : 0.3 * mm, "offsetDistance" : 25 * mm});
        }
        {
            var Q0;
            Q0=qCreatedBy(id+"F23.planeOp",FACE);
            var sketch = newSketch(context, id + "F26", { "sketchPlane" : qUnion([Q0])});
            skCircle(sketch, "E52", {"center": v(26.7, -26.7) * mm, "radius": 4 * mm});
            skLineSegment(sketch, "E53", {"start": v(26.7, -26.7) * mm, "end": v(26.7, 0) * mm, "construction": true});
            skLineSegment(sketch, "E54", {"start": v(26.7, -26.7) * mm, "end": v(0, -26.7) * mm, "construction": true});
            skSolve(sketch);
        }
        {
            var Q0;
            Q0 = qSketchRegion(id + "F26", true);
            extrude(context, id + "F27", {"entities" : qUnion([Q0]), "operationType" : NewBodyOperationType.ADD, "oppositeDirection" : true, "depth" : 19 * mm, "offsetDistance" : 25 * mm});
        }
        {
            var Q0;
            Q0=qCreatedBy(id+"F23.planeOp",FACE);
            var sketch = newSketch(context, id + "F28", { "sketchPlane" : qUnion([Q0])});
            skCircle(sketch, "E55", {"center": v(26.93, -26.93) * mm, "radius": 2.5 * mm});
            skLineSegment(sketch, "E56", {"start": v(26.93, -26.93) * mm, "end": v(26.93, 0) * mm, "construction": true});
            skLineSegment(sketch, "E57", {"start": v(26.93, -26.93) * mm, "end": v(0, -26.93) * mm, "construction": true});
            skSolve(sketch);
        }
        {
            var Q0;
            Q0 = qSketchRegion(id + "F28", true);
            extrude(context, id + "F29", {"entities" : qUnion([Q0]), "operationType" : NewBodyOperationType.REMOVE, "oppositeDirection" : true, "depth" : 19 * mm, "offsetDistance" : 25 * mm});
        }
    });
